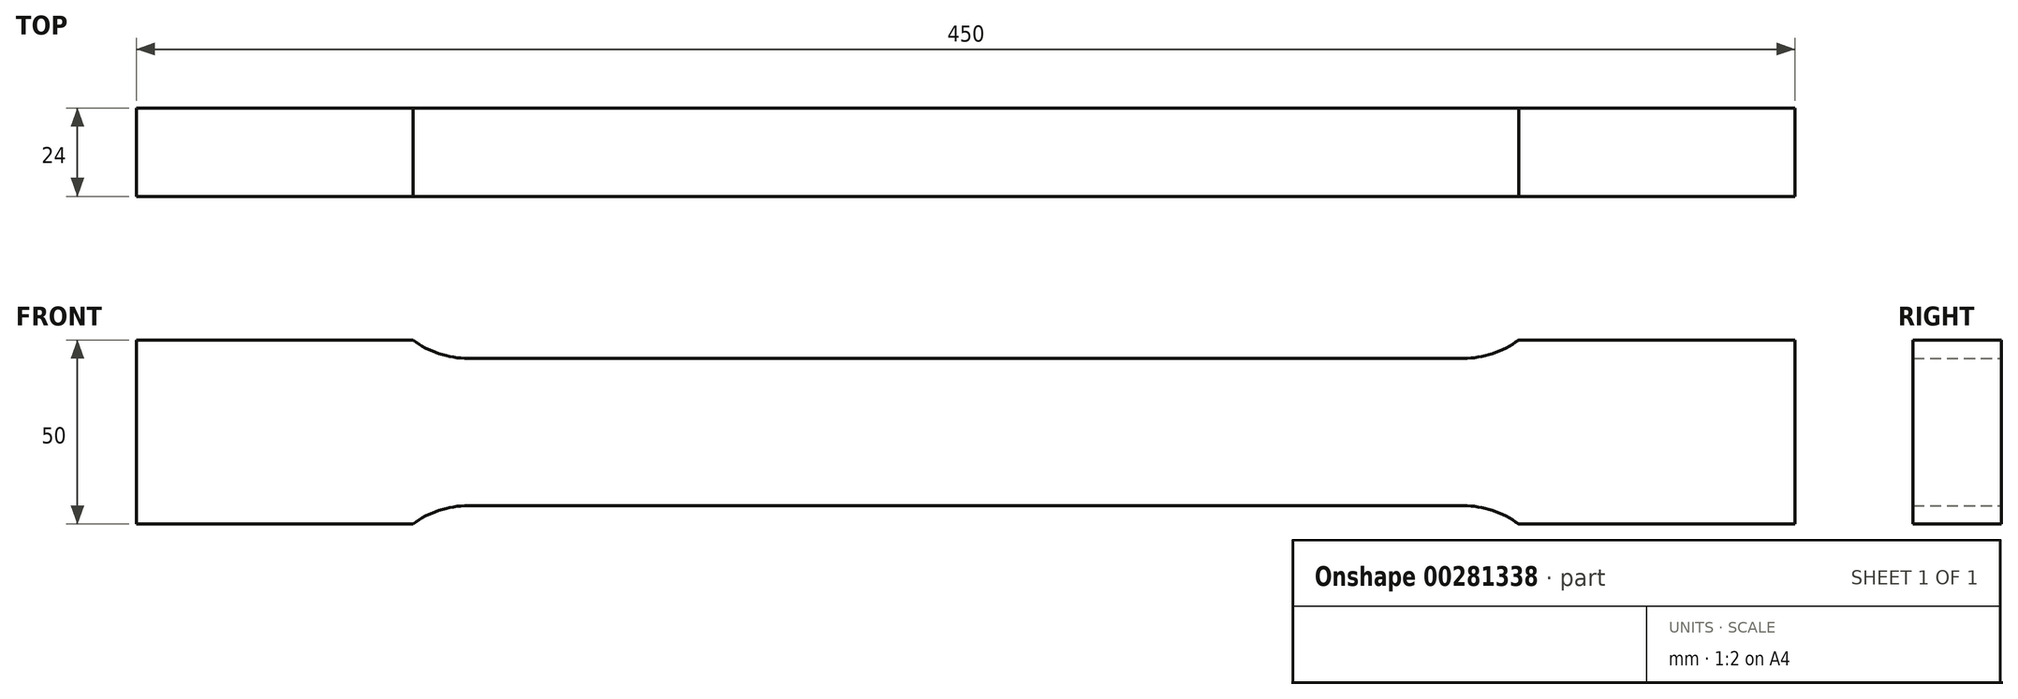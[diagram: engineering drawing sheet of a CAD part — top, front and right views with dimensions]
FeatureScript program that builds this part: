
annotation { "Feature Type Name" : "Feature", "Feature Type Description" : "" }
export const myFeature = defineFeature(function(context is Context, id is Id, definition is map)
    precondition{}
    {
        {
            var Q0;
            Q0=qCreatedBy(makeId("Front.planeOp"),FACE);
            var sketch = newSketch(context, id + "F0", { "sketchPlane" : qUnion([Q0])});
            skLineSegment(sketch, "E0", {"start": v(0, 20) * mm, "end": v(135, 20) * mm});
            skArc(sketch, "E1", {"start": v(135, 20) * mm, "mid": v(142.9, 21.28) * mm, "end": v(150, 25) * mm});
            skLineSegment(sketch, "E2", {"start": v(150, 25) * mm, "end": v(225, 25) * mm});
            skLineSegment(sketch, "E3", {"start": v(225, 25) * mm, "end": v(225, 0) * mm});
            skLineSegment(sketch, "E4.MirrorCS", {"start": v(0, -20) * mm, "end": v(135, -20) * mm});
            skLineSegment(sketch, "E5.MirrorCS", {"start": v(225, -25) * mm, "end": v(225, 0) * mm});
            skLineSegment(sketch, "E6.MirrorCS", {"start": v(150, -25) * mm, "end": v(225, -25) * mm});
            skArc(sketch, "E7.MirrorCS", {"start": v(135, -20) * mm, "mid": v(142.9, -21.28) * mm, "end": v(150, -25) * mm});
            skArc(sketch, "E8.MirrorCS", {"start": v(-135, -20) * mm, "mid": v(-142.9, -21.28) * mm, "end": v(-150, -25) * mm});
            skLineSegment(sketch, "E9.MirrorCS", {"start": v(-150, -25) * mm, "end": v(-225, -25) * mm});
            skArc(sketch, "E10.MirrorCS", {"start": v(-135, 20) * mm, "mid": v(-142.9, 21.28) * mm, "end": v(-150, 25) * mm});
            skLineSegment(sketch, "E11.MirrorCS", {"start": v(-150, 25) * mm, "end": v(-225, 25) * mm});
            skLineSegment(sketch, "E12.MirrorCS", {"start": v(-225, -25) * mm, "end": v(-225, 0) * mm});
            skLineSegment(sketch, "E13.MirrorCS", {"start": v(0, -20) * mm, "end": v(-135, -20) * mm});
            skLineSegment(sketch, "E14.MirrorCS", {"start": v(-225, 25) * mm, "end": v(-225, 0) * mm});
            skLineSegment(sketch, "E15.MirrorCS", {"start": v(0, 20) * mm, "end": v(-135, 20) * mm});
            skSolve(sketch);
        }
        {
            var Q0;
            Q0 = qSketchRegion(id + "F0", true);
            extrude(context, id + "F1", {"entities" : qUnion([Q0]), "depth" : 24 * mm});
        }
    });
